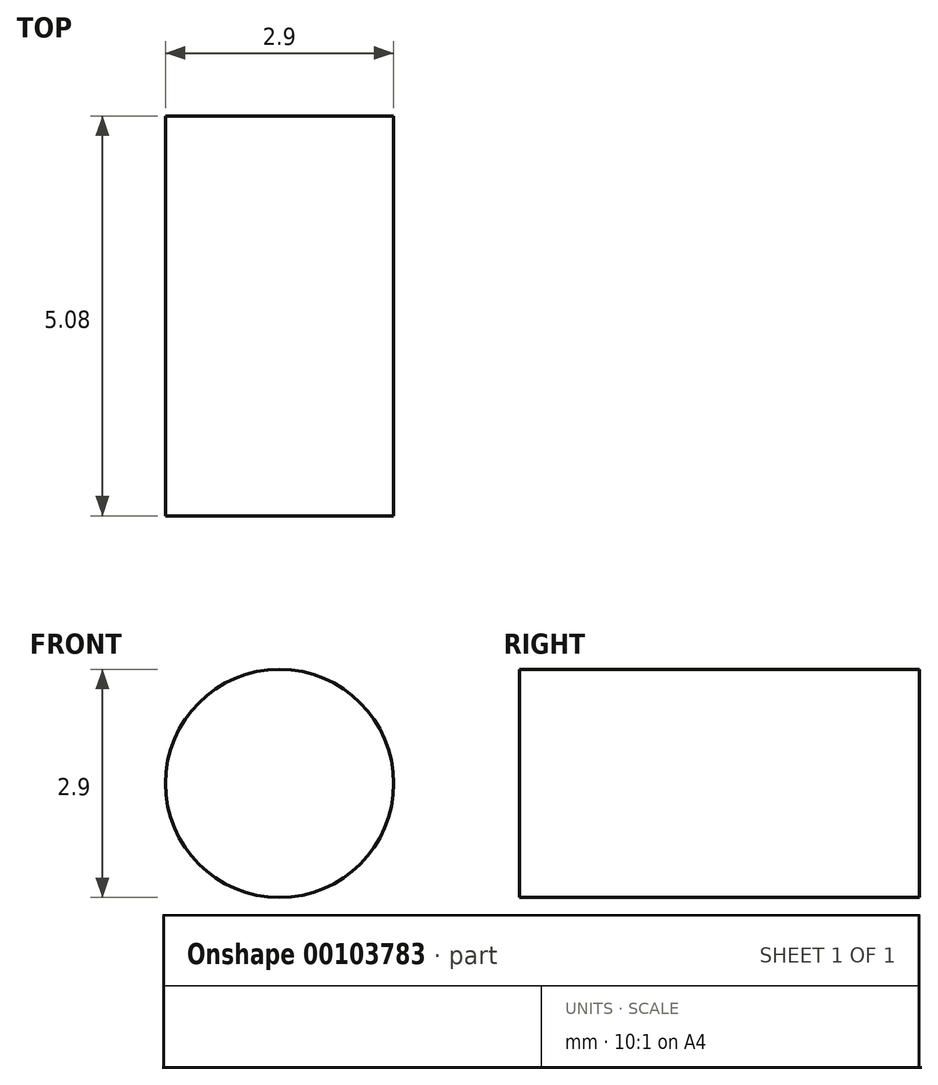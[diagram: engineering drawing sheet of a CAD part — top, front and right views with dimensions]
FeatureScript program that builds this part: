
annotation { "Feature Type Name" : "Feature", "Feature Type Description" : "" }
export const myFeature = defineFeature(function(context is Context, id is Id, definition is map)
    precondition{}
    {
        {
            var Q0;
            Q0=qCreatedBy(makeId("Front.planeOp"),FACE);
            var sketch = newSketch(context, id + "F0", { "sketchPlane" : qUnion([Q0])});
            skCircle(sketch, "E0", {"center": v(0, 0) * mm, "radius": 1.45 * mm});
            skSolve(sketch);
        }
        {
            var Q0;
            Q0=makeQuery(id+"F0.imprint","IMPRINT",FACE,{"disambiguationData":[TD([[makeQuery(id+"F0.imprint","IMPRINT",EDGE,{"derivedFrom":sQuery(id+"F0.wireOp",EDGE,"E0")}),1.0]])]});
            extrude(context, id + "F1", {"entities" : qUnion([Q0]), "depth" : 5.08 * mm});
        }
    });
